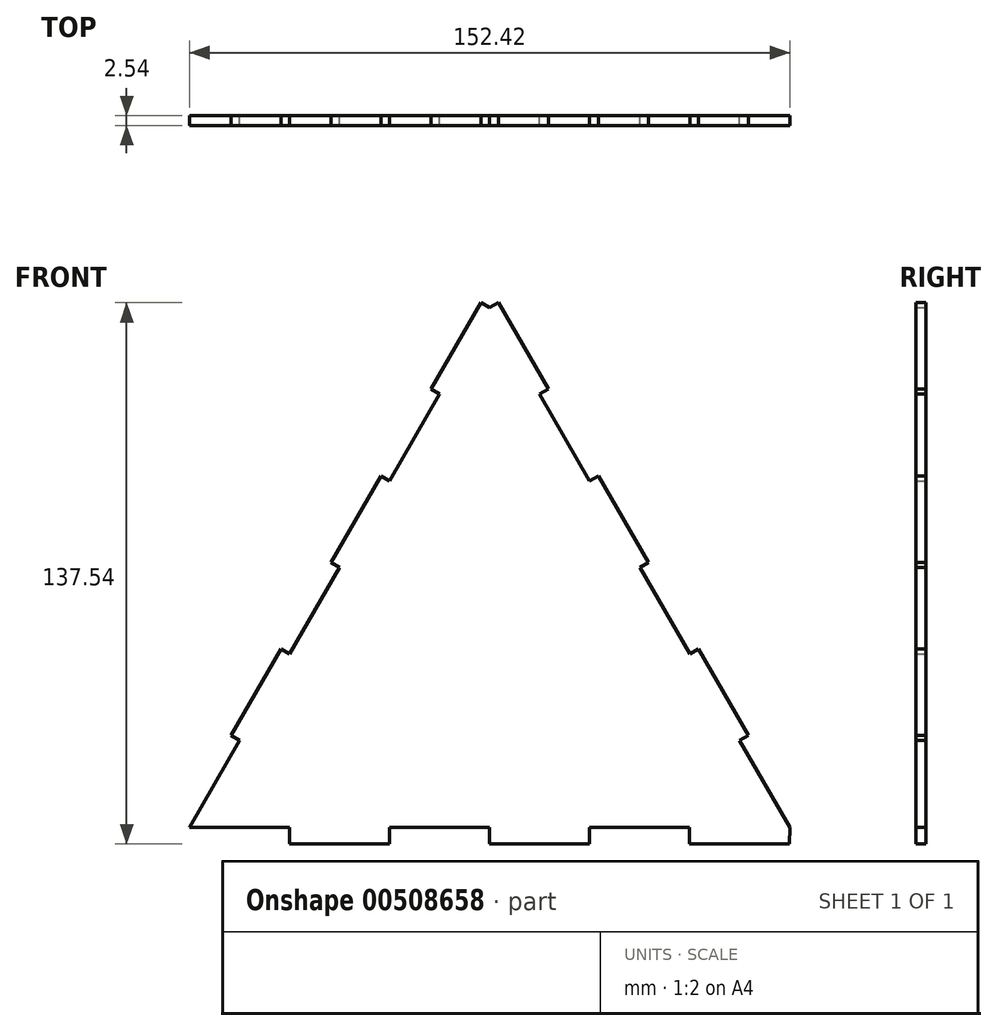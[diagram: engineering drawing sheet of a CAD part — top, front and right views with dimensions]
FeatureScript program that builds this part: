
annotation { "Feature Type Name" : "Feature", "Feature Type Description" : "" }
export const myFeature = defineFeature(function(context is Context, id is Id, definition is map)
    precondition{}
    {
        {
            var Q0;
            Q0=qCreatedBy(makeId("Front.planeOp"),FACE);
            var sketch = newSketch(context, id + "F0", { "sketchPlane" : qUnion([Q0])});
            skLineSegment(sketch, "E0", {"start": v(0, 62.62) * mm, "end": v(-76.21, -69.38) * mm});
            skLineSegment(sketch, "E1", {"start": v(-76.21, -69.38) * mm, "end": v(76.21, -69.38) * mm});
            skLineSegment(sketch, "E2", {"start": v(76.21, -69.38) * mm, "end": v(0, 62.62) * mm});
            skLineSegment(sketch, "E3", {"start": v(0, 62.62) * mm, "end": v(-2.2, 63.9) * mm});
            skLineSegment(sketch, "E4", {"start": v(-2.2, 63.9) * mm, "end": v(-14.9, 41.9) * mm});
            skLineSegment(sketch, "E5", {"start": v(-14.9, 41.9) * mm, "end": v(-12.7, 40.63) * mm});
            skLineSegment(sketch, "E6", {"start": v(-12.7, 40.63) * mm, "end": v(-25.4, 18.63) * mm});
            skLineSegment(sketch, "E7", {"start": v(-25.4, 18.63) * mm, "end": v(-27.6, 19.9) * mm});
            skLineSegment(sketch, "E8", {"start": v(-27.6, 19.9) * mm, "end": v(-40.3, -2.1) * mm});
            skLineSegment(sketch, "E9", {"start": v(-40.3, -2.1) * mm, "end": v(-38.1, -3.37) * mm});
            skLineSegment(sketch, "E10", {"start": v(-38.1, -3.37) * mm, "end": v(-50.8, -25.36) * mm});
            skLineSegment(sketch, "E11", {"start": v(-50.8, -25.36) * mm, "end": v(-53, -24.1) * mm});
            skLineSegment(sketch, "E12", {"start": v(-53, -24.1) * mm, "end": v(-65.7, -46.1) * mm});
            skLineSegment(sketch, "E13", {"start": v(-65.7, -46.1) * mm, "end": v(-63.5, -47.36) * mm});
            skLineSegment(sketch, "E14", {"start": v(-76.21, -69.38) * mm, "end": v(-50.81, -69.38) * mm});
            skLineSegment(sketch, "E15", {"start": v(-50.81, -69.38) * mm, "end": v(-50.81, -73.65) * mm});
            skLineSegment(sketch, "E16", {"start": v(-50.81, -73.65) * mm, "end": v(-25.41, -73.65) * mm});
            skLineSegment(sketch, "E17", {"start": v(-25.41, -73.65) * mm, "end": v(-25.41, -69.38) * mm});
            skLineSegment(sketch, "E18", {"start": v(-25.41, -69.38) * mm, "end": v(0, -69.38) * mm});
            skLineSegment(sketch, "E19", {"start": v(0, -69.38) * mm, "end": v(0, -73.65) * mm});
            skLineSegment(sketch, "E20", {"start": v(0, -73.65) * mm, "end": v(25.4, -73.65) * mm});
            skLineSegment(sketch, "E21", {"start": v(25.4, -73.65) * mm, "end": v(25.4, -69.38) * mm});
            skLineSegment(sketch, "E22", {"start": v(25.4, -69.38) * mm, "end": v(50.8, -69.38) * mm});
            skLineSegment(sketch, "E23", {"start": v(50.8, -69.38) * mm, "end": v(50.8, -73.65) * mm});
            skLineSegment(sketch, "E24", {"start": v(50.8, -73.65) * mm, "end": v(76.2, -73.65) * mm});
            skLineSegment(sketch, "E25", {"start": v(76.2, -73.65) * mm, "end": v(76.21, -69.38) * mm});
            skLineSegment(sketch, "E26", {"start": v(76.21, -69.38) * mm, "end": v(63.5, -47.37) * mm});
            skLineSegment(sketch, "E27", {"start": v(63.5, -47.37) * mm, "end": v(65.7, -46.1) * mm});
            skLineSegment(sketch, "E28", {"start": v(65.7, -46.1) * mm, "end": v(53, -24.1) * mm});
            skLineSegment(sketch, "E29", {"start": v(53, -24.1) * mm, "end": v(50.8, -25.37) * mm});
            skLineSegment(sketch, "E30", {"start": v(50.8, -25.37) * mm, "end": v(38.1, -3.38) * mm});
            skLineSegment(sketch, "E31", {"start": v(38.1, -3.38) * mm, "end": v(40.3, -2.1) * mm});
            skLineSegment(sketch, "E32", {"start": v(40.3, -2.1) * mm, "end": v(27.6, 19.9) * mm});
            skLineSegment(sketch, "E33", {"start": v(27.6, 19.9) * mm, "end": v(25.4, 18.63) * mm});
            skLineSegment(sketch, "E34", {"start": v(25.4, 18.63) * mm, "end": v(12.7, 40.63) * mm});
            skLineSegment(sketch, "E35", {"start": v(12.7, 40.63) * mm, "end": v(14.9, 41.9) * mm});
            skLineSegment(sketch, "E36", {"start": v(0, 62.62) * mm, "end": v(2.2, 63.9) * mm});
            skLineSegment(sketch, "E37", {"start": v(2.2, 63.9) * mm, "end": v(14.9, 41.9) * mm});
            skSolve(sketch);
        }
        {
            var Q0;
            Q0 = qSketchRegion(id + "F0", true);
            extrude(context, id + "F1", {"entities" : qUnion([Q0]), "depth" : 2.54 * mm, "offsetDistance" : 25.4 * mm});
        }
    });
